# Revit family: QF_MACOM_BM91C-N_G
name_source: partatom
category: Equipamento especial
units: mm (PartAtom-declared; Revit-internal decimal feet)

## family parameters
Com base no plano de trabalho = Não
Compartilhado = Não
Corte com vazios quando carregada = Não
Cota do conector redondo = Utilizar diâmetro
Número OmniClass = 23.40.40.14.17.11
Ponto de cálculo do ambiente = Não
Sempre na vertical = Sim
Tipo de parte = Normal
Título OmniClass = Cookers, Ovens, Stoves

## types (2) — shared parameters
Capacity in Litres = 32,7 L
Cycle = 60 Hz
Depth = 972 mm
Elec Connection Height = 50 mm
Electric Power = 0 W
Elevação padrão = 0 mm
Fabricante = MACOM
Gas Pressure = 0,0 bar
Gas Size = 3/4"
Height = 286 mm
Ingress Protection Code = IP 22
Length = 450 mm
URL = https://www.acosmacom.com.br
Volts = 220 V
Volume = 0,13 m³
Weight = 35 kg
Work Temperature = +20°C to +85°C

## per-type parameters (varying)
| type | Descrição | Gas Connection Height | Gas Consumption GLP | Gas Consumption GN | Gas Input GLP | Gas Input GN |
| BM91C-G | BANHO-MARIA A GLP NATURAL 900HP MACOM - 450X972X265MM | 61 mm | 0,43 Kg/h | 0,0 m³/h | 19758 Btu/h |  |
| BM91C-N | BANHO-MARIA A GAS NATURAL 900HP MACOM - 450X972X265MM | 81 mm |  | 0,5 m³/h | 0 Btu/h | 4979 Kcal/h |

note: column(s) folded — value = type name in every type: Modelo

## geometry (parser evidence)
native form markers: Sweep x9
no freeform markers — native parametric forms only
